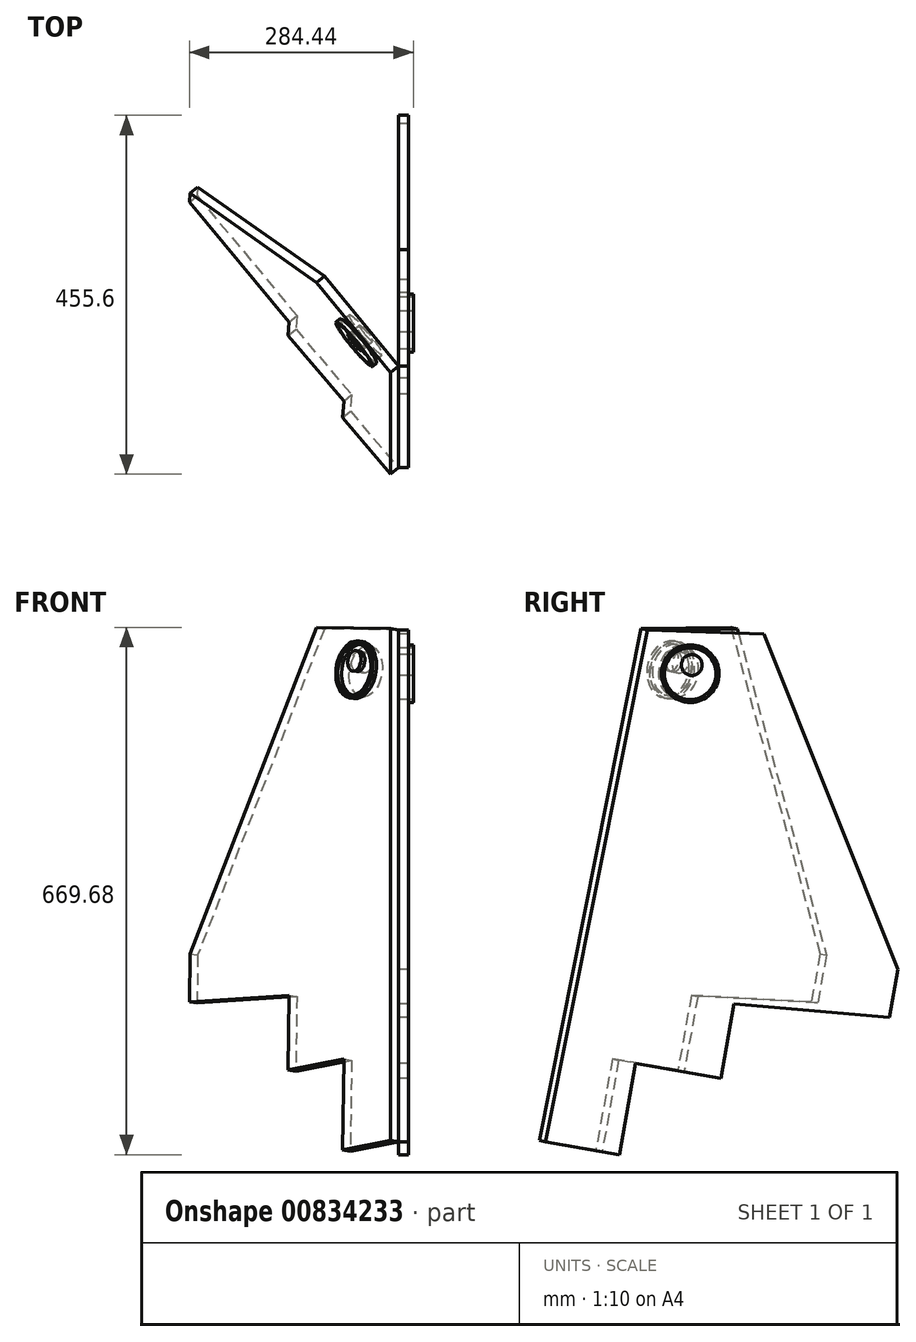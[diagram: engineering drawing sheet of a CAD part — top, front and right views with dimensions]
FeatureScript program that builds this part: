
annotation { "Feature Type Name" : "Feature", "Feature Type Description" : "" }
export const myFeature = defineFeature(function(context is Context, id is Id, definition is map)
    precondition{}
    {
        {
            var Q0;
            Q0=qCreatedBy(makeId("Right.planeOp"),FACE);
            var sketch = newSketch(context, id + "F0", { "sketchPlane" : qUnion([Q0])});
            skLineSegment(sketch, "E0", {"start": v(-405.1, 388.6) * mm, "end": v(-258.5, 409.1) * mm});
            skLineSegment(sketch, "E1", {"start": v(-258.5, 409.1) * mm, "end": v(-16.51, 19.2) * mm});
            skLineSegment(sketch, "E2", {"start": v(-16.51, 19.2) * mm, "end": v(-16.51, -42.74) * mm});
            skLineSegment(sketch, "E3", {"start": v(-16.51, -42.74) * mm, "end": v(-214.12, -60) * mm});
            skLineSegment(sketch, "E4", {"start": v(-214.12, -60) * mm, "end": v(-214.12, -156.47) * mm});
            skLineSegment(sketch, "E5", {"start": v(-214.12, -156.47) * mm, "end": v(-324.25, -156.47) * mm});
            skLineSegment(sketch, "E6", {"start": v(-324.25, -156.47) * mm, "end": v(-324.25, -274.12) * mm});
            skLineSegment(sketch, "E7", {"start": v(-324.25, -274.12) * mm, "end": v(-419.29, -274.12) * mm});
            skLineSegment(sketch, "E8", {"start": v(-419.29, -274.12) * mm, "end": v(-405.1, 388.6) * mm});
            skLineSegment(sketch, "E9", {"start": v(-258.5, 409.1) * mm, "end": v(-258.5, -276.7) * mm});
            skCircle(sketch, "E10", {"center": v(-341.6, 343.36) * mm, "radius": 32.77 * mm});
            skCircle(sketch, "E11", {"center": v(-341.6, 354.46) * mm, "radius": 13.15 * mm});
            skCircle(sketch, "E12.0", {"center": v(-341.6, 343.36) * mm, "radius": 36.58 * mm});
            skSolve(sketch);
        }
        {
            var Q0;
            {var subQ1=sQuery(id+"F0.wireOp",EDGE,"E1");Q0=makeQuery(id+"F0.imprint","IMPRINT",FACE,{"disambiguationData":[TD([[makeQuery(id+"F0.imprint","IMPRINT",EDGE,{"derivedFrom":subQ1}),-1.0]])]});}
            var Q1;
            {var subQ4=sQuery(id+"F0.wireOp",EDGE,"E0");Q1=makeQuery(id+"F0.imprint","IMPRINT",FACE,{"disambiguationData":[TD([[makeQuery(id+"F0.imprint","IMPRINT",EDGE,{"derivedFrom":subQ4}),-1.0]])]});}
            extrude(context, id + "F1", {"entities" : qUnion([Q0, Q1]), "depth" : 12.7 * mm, "offsetDistance" : 25.4 * mm});
        }
        {
            var Q0;
            Q0=makeQuery(id+"F0.imprint","IMPRINT",FACE,{"disambiguationData":[TD([[makeQuery(id+"F0.imprint","IMPRINT",EDGE,{"derivedFrom":sQuery(id+"F0.wireOp",EDGE,"E10")}),-1.0]])]});
            var Q1;
            Q1=makeQuery(id+"F0.imprint","IMPRINT",FACE,{"disambiguationData":[TD([[makeQuery(id+"F0.imprint","IMPRINT",EDGE,{"derivedFrom":sQuery(id+"F0.wireOp",EDGE,"E11")}),1.0]])]});
            extrude(context, id + "F2", {"entities" : qUnion([Q0, Q1]), "operationType" : NewBodyOperationType.ADD, "depth" : 19.05 * mm, "offsetDistance" : 25.4 * mm});
        }
        {
            var Q0;
            Q0=makeQuery(id+"F0.imprint","IMPRINT",FACE,{"disambiguationData":[TD([[makeQuery(id+"F0.imprint","IMPRINT",EDGE,{"derivedFrom":sQuery(id+"F0.wireOp",EDGE,"E10")}),1.0]])]});
            extrude(context, id + "F3", {"entities" : qUnion([Q0]), "depth" : 12.7 * mm, "offsetDistance" : 25.4 * mm});
        }
        {
            var Q0;
            Q0=makeQuery(id+"F2.opExtrude","SWEPT_BODY",BODY,{"disambiguationData":[OSD([sQuery(id+"F0.wireOp",EDGE,"E11")])]});
            var Q1;
            Q1=makeQuery(id+"F3.opExtrude","SWEPT_BODY",BODY,{"disambiguationData":[OSD([sQuery(id+"F0.wireOp",EDGE,"E10"),sQuery(id+"F0.wireOp",EDGE,"E11")])]});
            var Q2;
            Q2=makeQuery(id+"F1.opExtrude","SWEPT_BODY",BODY,{"disambiguationData":[OSD([sQuery(id+"F0.wireOp",EDGE,"E0"),sQuery(id+"F0.wireOp",EDGE,"E1"),sQuery(id+"F0.wireOp",EDGE,"E2"),sQuery(id+"F0.wireOp",EDGE,"E3"),sQuery(id+"F0.wireOp",EDGE,"E4"),sQuery(id+"F0.wireOp",EDGE,"E5"),sQuery(id+"F0.wireOp",EDGE,"E6"),sQuery(id+"F0.wireOp",EDGE,"E7"),sQuery(id+"F0.wireOp",EDGE,"E8"),sQuery(id+"F0.wireOp",EDGE,"E12.0")])]});
            var Q3;
            Q3=qCreatedBy(makeId("Right.planeOp"),FACE);
            mirror(context, id + "F4", {"entities" : qUnion([Q0, Q1, Q2]), "mirrorPlane" : qUnion([Q3])});
        }
        {
            var Q0;
            Q0=makeQuery(id+"F4.opPattern","COPY",BODY,{"derivedFrom":makeQuery(id+"F1.opExtrude","SWEPT_BODY",BODY,{"disambiguationData":[OSD([sQuery(id+"F0.wireOp",EDGE,"E0"),sQuery(id+"F0.wireOp",EDGE,"E1"),sQuery(id+"F0.wireOp",EDGE,"E2"),sQuery(id+"F0.wireOp",EDGE,"E3"),sQuery(id+"F0.wireOp",EDGE,"E4"),sQuery(id+"F0.wireOp",EDGE,"E5"),sQuery(id+"F0.wireOp",EDGE,"E6"),sQuery(id+"F0.wireOp",EDGE,"E7"),sQuery(id+"F0.wireOp",EDGE,"E8"),sQuery(id+"F0.wireOp",EDGE,"E12.0")])]}),"instanceName":"1"});
            var Q1;
            Q1=makeQuery(id+"F4.opPattern","COPY",BODY,{"derivedFrom":makeQuery(id+"F3.opExtrude","SWEPT_BODY",BODY,{"disambiguationData":[OSD([sQuery(id+"F0.wireOp",EDGE,"E10"),sQuery(id+"F0.wireOp",EDGE,"E11")])]}),"instanceName":"1"});
            var Q2;
            Q2=makeQuery(id+"F4.opPattern","COPY",BODY,{"derivedFrom":makeQuery(id+"F2.opExtrude","SWEPT_BODY",BODY,{"disambiguationData":[OSD([sQuery(id+"F0.wireOp",EDGE,"E11")])]}),"instanceName":"1"});
            var Q3;
            Q3=qCreatedBy(makeId("Right.planeOp"),FACE);
            transform(context, id + "F5", {"entities" : qUnion([Q0, Q1, Q2]), "transformType" : TransformType.TRANSLATION_DISTANCE, "transformDirection" : qUnion([Q3]), "distance" : 101.6 * mm, "oppositeDirection" : true, "makeCopy" : false});
        }
        {
            var Q0;
            Q0=makeQuery(id+"F4.opPattern","COPY",BODY,{"derivedFrom":makeQuery(id+"F1.opExtrude","SWEPT_BODY",BODY,{"disambiguationData":[OSD([sQuery(id+"F0.wireOp",EDGE,"E0"),sQuery(id+"F0.wireOp",EDGE,"E1"),sQuery(id+"F0.wireOp",EDGE,"E2"),sQuery(id+"F0.wireOp",EDGE,"E3"),sQuery(id+"F0.wireOp",EDGE,"E4"),sQuery(id+"F0.wireOp",EDGE,"E5"),sQuery(id+"F0.wireOp",EDGE,"E6"),sQuery(id+"F0.wireOp",EDGE,"E7"),sQuery(id+"F0.wireOp",EDGE,"E8"),sQuery(id+"F0.wireOp",EDGE,"E12.0")])]}),"instanceName":"1"});
            var Q1;
            Q1=makeQuery(id+"F4.opPattern","COPY",BODY,{"derivedFrom":makeQuery(id+"F2.opExtrude","SWEPT_BODY",BODY,{"disambiguationData":[OSD([sQuery(id+"F0.wireOp",EDGE,"E11")])]}),"instanceName":"1"});
            var Q2;
            Q2=makeQuery(id+"F4.opPattern","COPY",BODY,{"derivedFrom":makeQuery(id+"F3.opExtrude","SWEPT_BODY",BODY,{"disambiguationData":[OSD([sQuery(id+"F0.wireOp",EDGE,"E10"),sQuery(id+"F0.wireOp",EDGE,"E11")])]}),"instanceName":"1"});
            var Q3;
            Q3=makeQuery(id+"F4.opPattern","COPY",EDGE,{"derivedFrom":makeQuery(id+"F1.opExtrude","CAP_EDGE",EDGE,{"disambiguationData":[OSD([sQuery(id+"F0.wireOp",EDGE,"E8")])],"isStart":true}),"instanceName":"1"});
            transform(context, id + "F6", {"entities" : qUnion([Q0, Q1, Q2]), "transformType" : TransformType.ROTATION, "transformAxis" : qUnion([Q3]), "angle" : 40 * degree, "makeCopy" : false});
        }
        {
            var Q0;
            Q0=makeQuery(id+"F4.opPattern","COPY",BODY,{"derivedFrom":makeQuery(id+"F2.opExtrude","SWEPT_BODY",BODY,{"disambiguationData":[OSD([sQuery(id+"F0.wireOp",EDGE,"E11")])]}),"instanceName":"1"});
            var Q1;
            Q1=makeQuery(id+"F4.opPattern","COPY",BODY,{"derivedFrom":makeQuery(id+"F1.opExtrude","SWEPT_BODY",BODY,{"disambiguationData":[OSD([sQuery(id+"F0.wireOp",EDGE,"E0"),sQuery(id+"F0.wireOp",EDGE,"E1"),sQuery(id+"F0.wireOp",EDGE,"E2"),sQuery(id+"F0.wireOp",EDGE,"E3"),sQuery(id+"F0.wireOp",EDGE,"E4"),sQuery(id+"F0.wireOp",EDGE,"E5"),sQuery(id+"F0.wireOp",EDGE,"E6"),sQuery(id+"F0.wireOp",EDGE,"E7"),sQuery(id+"F0.wireOp",EDGE,"E8"),sQuery(id+"F0.wireOp",EDGE,"E12.0")])]}),"instanceName":"1"});
            var Q2;
            Q2=makeQuery(id+"F4.opPattern","COPY",BODY,{"derivedFrom":makeQuery(id+"F3.opExtrude","SWEPT_BODY",BODY,{"disambiguationData":[OSD([sQuery(id+"F0.wireOp",EDGE,"E10"),sQuery(id+"F0.wireOp",EDGE,"E11")])]}),"instanceName":"1"});
            transform(context, id + "F7", {"entities" : qUnion([Q0, Q1, Q2]), "transformType" : TransformType.TRANSLATION_3D, "dx" : 101.6 * mm, "dy" : 0 * mm, "dz" : 0 * mm, "makeCopy" : false});
        }
        {
            var Q0;
            Q0=makeQuery(id+"F4.opPattern","COPY",BODY,{"derivedFrom":makeQuery(id+"F2.opExtrude","SWEPT_BODY",BODY,{"disambiguationData":[OSD([sQuery(id+"F0.wireOp",EDGE,"E11")])]}),"instanceName":"1"});
            var Q1;
            Q1=makeQuery(id+"F1.opExtrude","SWEPT_BODY",BODY,{"disambiguationData":[OSD([sQuery(id+"F0.wireOp",EDGE,"E0"),sQuery(id+"F0.wireOp",EDGE,"E1"),sQuery(id+"F0.wireOp",EDGE,"E2"),sQuery(id+"F0.wireOp",EDGE,"E3"),sQuery(id+"F0.wireOp",EDGE,"E4"),sQuery(id+"F0.wireOp",EDGE,"E5"),sQuery(id+"F0.wireOp",EDGE,"E6"),sQuery(id+"F0.wireOp",EDGE,"E7"),sQuery(id+"F0.wireOp",EDGE,"E8"),sQuery(id+"F0.wireOp",EDGE,"E12.0")])]});
            var Q2;
            Q2=makeQuery(id+"F3.opExtrude","SWEPT_BODY",BODY,{"disambiguationData":[OSD([sQuery(id+"F0.wireOp",EDGE,"E10"),sQuery(id+"F0.wireOp",EDGE,"E11")])]});
            var Q3;
            Q3=makeQuery(id+"F4.opPattern","COPY",BODY,{"derivedFrom":makeQuery(id+"F1.opExtrude","SWEPT_BODY",BODY,{"disambiguationData":[OSD([sQuery(id+"F0.wireOp",EDGE,"E0"),sQuery(id+"F0.wireOp",EDGE,"E1"),sQuery(id+"F0.wireOp",EDGE,"E2"),sQuery(id+"F0.wireOp",EDGE,"E3"),sQuery(id+"F0.wireOp",EDGE,"E4"),sQuery(id+"F0.wireOp",EDGE,"E5"),sQuery(id+"F0.wireOp",EDGE,"E6"),sQuery(id+"F0.wireOp",EDGE,"E7"),sQuery(id+"F0.wireOp",EDGE,"E8"),sQuery(id+"F0.wireOp",EDGE,"E12.0")])]}),"instanceName":"1"});
            var Q4;
            Q4=makeQuery(id+"F4.opPattern","COPY",BODY,{"derivedFrom":makeQuery(id+"F3.opExtrude","SWEPT_BODY",BODY,{"disambiguationData":[OSD([sQuery(id+"F0.wireOp",EDGE,"E10"),sQuery(id+"F0.wireOp",EDGE,"E11")])]}),"instanceName":"1"});
            var Q5;
            Q5=makeQuery(id+"F2.opExtrude","SWEPT_BODY",BODY,{"disambiguationData":[OSD([sQuery(id+"F0.wireOp",EDGE,"E11")])]});
            transform(context, id + "F8", {"entities" : qUnion([Q0, Q1, Q2, Q3, Q4, Q5]), "transformType" : TransformType.TRANSLATION_3D, "dx" : 63.5 * mm, "dy" : 317.5 * mm, "dz" : -259.08 * mm, "makeCopy" : false});
        }
        {
            var Q0;
            Q0=makeQuery(id+"F1.opExtrude","SWEPT_BODY",BODY,{"disambiguationData":[OSD([sQuery(id+"F0.wireOp",EDGE,"E0"),sQuery(id+"F0.wireOp",EDGE,"E1"),sQuery(id+"F0.wireOp",EDGE,"E2"),sQuery(id+"F0.wireOp",EDGE,"E3"),sQuery(id+"F0.wireOp",EDGE,"E4"),sQuery(id+"F0.wireOp",EDGE,"E5"),sQuery(id+"F0.wireOp",EDGE,"E6"),sQuery(id+"F0.wireOp",EDGE,"E7"),sQuery(id+"F0.wireOp",EDGE,"E8"),sQuery(id+"F0.wireOp",EDGE,"E12.0")])]});
            var Q1;
            Q1=makeQuery(id+"F3.opExtrude","SWEPT_BODY",BODY,{"disambiguationData":[OSD([sQuery(id+"F0.wireOp",EDGE,"E10"),sQuery(id+"F0.wireOp",EDGE,"E11")])]});
            var Q2;
            Q2=makeQuery(id+"F2.opExtrude","SWEPT_BODY",BODY,{"disambiguationData":[OSD([sQuery(id+"F0.wireOp",EDGE,"E11")])]});
            var Q3;
            Q3=makeQuery(id+"F4.opPattern","COPY",BODY,{"derivedFrom":makeQuery(id+"F1.opExtrude","SWEPT_BODY",BODY,{"disambiguationData":[OSD([sQuery(id+"F0.wireOp",EDGE,"E0"),sQuery(id+"F0.wireOp",EDGE,"E1"),sQuery(id+"F0.wireOp",EDGE,"E2"),sQuery(id+"F0.wireOp",EDGE,"E3"),sQuery(id+"F0.wireOp",EDGE,"E4"),sQuery(id+"F0.wireOp",EDGE,"E5"),sQuery(id+"F0.wireOp",EDGE,"E6"),sQuery(id+"F0.wireOp",EDGE,"E7"),sQuery(id+"F0.wireOp",EDGE,"E8"),sQuery(id+"F0.wireOp",EDGE,"E12.0")])]}),"instanceName":"1"});
            var Q4;
            Q4=makeQuery(id+"F4.opPattern","COPY",BODY,{"derivedFrom":makeQuery(id+"F2.opExtrude","SWEPT_BODY",BODY,{"disambiguationData":[OSD([sQuery(id+"F0.wireOp",EDGE,"E11")])]}),"instanceName":"1"});
            var Q5;
            Q5=makeQuery(id+"F4.opPattern","COPY",BODY,{"derivedFrom":makeQuery(id+"F3.opExtrude","SWEPT_BODY",BODY,{"disambiguationData":[OSD([sQuery(id+"F0.wireOp",EDGE,"E10"),sQuery(id+"F0.wireOp",EDGE,"E11")])]}),"instanceName":"1"});
            var Q6;
            Q6=makeQuery(id+"F1.opExtrude","SWEPT_EDGE",EDGE,{"disambiguationData":[OSD([sQuery(id+"F0.wireOp",EDGE,"E0"),sQuery(id+"F0.wireOp",EDGE,"E8")])]});
            transform(context, id + "F9", {"entities" : qUnion([Q0, Q1, Q2, Q3, Q4, Q5]), "transformType" : TransformType.ROTATION, "transformAxis" : qUnion([Q6]), "angle" : 10 * degree, "makeCopy" : false});
        }
    });
